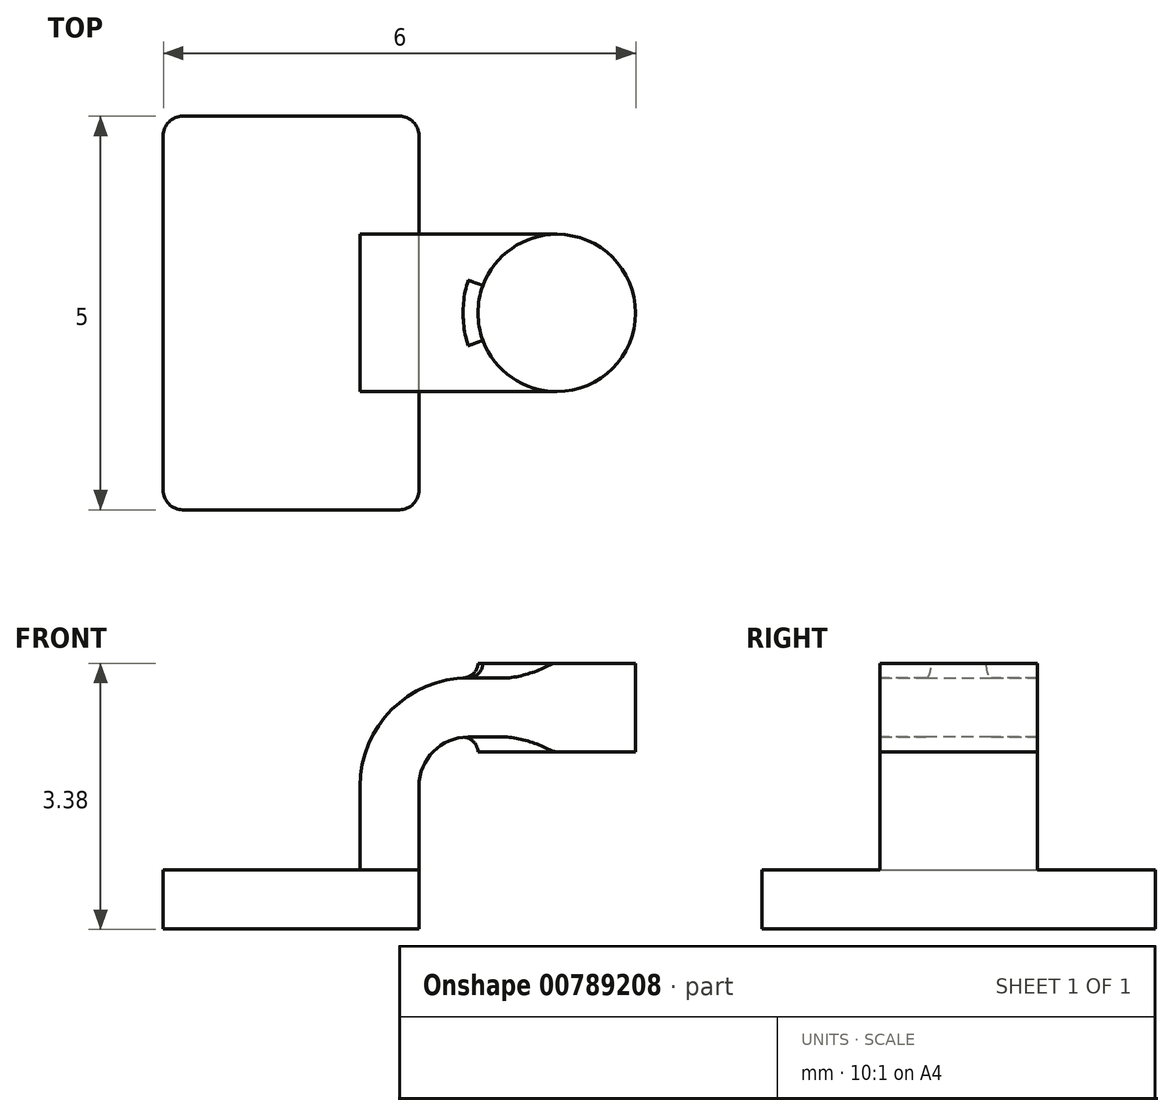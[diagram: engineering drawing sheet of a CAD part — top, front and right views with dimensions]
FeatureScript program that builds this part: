
annotation { "Feature Type Name" : "Feature", "Feature Type Description" : "" }
export const myFeature = defineFeature(function(context is Context, id is Id, definition is map)
    precondition{}
    {
        {
            var Q0;
            Q0=qCreatedBy(makeId("Front.planeOp"),FACE);
            var sketch = newSketch(context, id + "F0", { "sketchPlane" : qUnion([Q0])});
            skLineSegment(sketch, "E0.bottom", {"start": v(-1.63, 0.38) * mm, "end": v(1.63, 0.38) * mm});
            skLineSegment(sketch, "E0.top", {"start": v(-1.63, -0.38) * mm, "end": v(1.63, -0.38) * mm});
            skLineSegment(sketch, "E0.left", {"start": v(-1.62, 0.38) * mm, "end": v(-1.62, -0.38) * mm});
            skLineSegment(sketch, "E0.right", {"start": v(1.63, 0.37) * mm, "end": v(1.63, -0.38) * mm});
            skPoint(sketch, "E0.middle", {"position": v(0, 0) * mm});
            skLineSegment(sketch, "E1.bottom", {"start": v(4.38, 1.87) * mm, "end": v(2.38, 1.87) * mm});
            skLineSegment(sketch, "E1.top", {"start": v(4.37, 3) * mm, "end": v(2.38, 3) * mm});
            skLineSegment(sketch, "E1.left", {"start": v(4.38, 1.87) * mm, "end": v(4.37, 3) * mm});
            skLineSegment(sketch, "E1.right", {"start": v(2.38, 1.88) * mm, "end": v(2.38, 3) * mm});
            skPoint(sketch, "E1.middle", {"position": v(3.38, 2.44) * mm});
            skLineSegment(sketch, "E2", {"start": v(1.62, 0.38) * mm, "end": v(1.62, 1.44) * mm});
            skArc(sketch, "E3", {"start": v(1.62, 1.44) * mm, "mid": v(1.8, 1.88) * mm, "end": v(2.25, 2.06) * mm});
            skLineSegment(sketch, "E4", {"start": v(2.25, 2.06) * mm, "end": v(3.38, 2.06) * mm});
            skLineSegment(sketch, "E5.0", {"start": v(2.25, 2.81) * mm, "end": v(3.38, 2.81) * mm});
            skArc(sketch, "E5.1", {"start": v(0.87, 1.44) * mm, "mid": v(1.28, 2.41) * mm, "end": v(2.25, 2.81) * mm});
            skLineSegment(sketch, "E5.2", {"start": v(0.87, 0.38) * mm, "end": v(0.87, 1.44) * mm});
            skLineSegment(sketch, "E6", {"start": v(3.38, 1.87) * mm, "end": v(3.38, 3) * mm});
            skFitSpline(sketch, "E7", {"points": [v(-1.62, 0.38) * mm, v(2.25, 2.81) * mm], "startDerivative": vector(0.08, 3.8) * mm, "endDerivative": vector(8.07, -0.01) * mm});
            skSolve(sketch);
        }
        {
            var Q0;
            Q0=makeQuery(id+"F0.imprint","IMPRINT",FACE,{"disambiguationData":[TD([[makeQuery(id+"F0.imprint","IMPRINT",EDGE,{"derivedFrom":sQuery(id+"F0.wireOp",EDGE,"E0.top")}),1.0]])]});
            extrude(context, id + "F1", {"entities" : qUnion([Q0]), "endBound" : BoundingType.SYMMETRIC, "depth" : 5 * mm, "offsetDistance" : 25 * mm});
        }
        {
            var Q0;
            {var subQ1=sQuery(id+"F0.wireOp",EDGE,"E2");Q0=makeQuery(id+"F0.imprint","IMPRINT",FACE,{"disambiguationData":[TD([[makeQuery(id+"F0.imprint","IMPRINT",EDGE,{"derivedFrom":subQ1}),1.0]])]});}
            var Q1;
            {var subQ0=sQuery(id+"F0.wireOp",EDGE,"E4");var subQ1=sQuery(id+"F0.wireOp",EDGE,"E1.right");var subQ2=makeQuery(id+"F0.imprint","INTERSECT",VERTEX,{"derivedFrom":[subQ1,subQ0]});Q1=makeQuery(id+"F0.imprint","IMPRINT",FACE,{"disambiguationData":[TD([[makeQuery(id+"F0.imprint","IMPRINT",EDGE,{"disambiguationData":[TD([[subQ2,-1.0]])],"derivedFrom":subQ1}),-1.0]])]});}
            extrude(context, id + "F2", {"entities" : qUnion([Q0, Q1]), "operationType" : NewBodyOperationType.ADD, "endBound" : BoundingType.SYMMETRIC, "depth" : 2 * mm, "offsetDistance" : 25 * mm});
        }
        {
            var Q0;
            Q0=makeQuery(id+"F0.imprint","IMPRINT",FACE,{"disambiguationData":[TD([[makeQuery(id+"F0.imprint","IMPRINT",EDGE,{"derivedFrom":sQuery(id+"F0.wireOp",EDGE,"E5.1")}),1.0]])]});
            extrude(context, id + "F3", {"entities" : qUnion([Q0]), "operationType" : NewBodyOperationType.ADD, "endBound" : BoundingType.SYMMETRIC, "depth" : 0.62 * mm, "offsetDistance" : 25 * mm});
        }
        {
            var Q0;
            {var subQ4=sQuery(id+"F0.wireOp",EDGE,"E1.left");Q0=makeQuery(id+"F0.imprint","IMPRINT",FACE,{"disambiguationData":[TD([[makeQuery(id+"F0.imprint","IMPRINT",EDGE,{"derivedFrom":subQ4}),1.0]])]});}
            var Q1;
            Q1=sQuery(id+"F0.wireOp",EDGE,"E6");
            revolve(context, id + "F4", {"operationType" : NewBodyOperationType.ADD, "surfaceOperationType" : NewSurfaceOperationType.NEW, "entities" : qUnion([Q0]), "axis" : qUnion([Q1]), "revolveType" : RevolveType.FULL});
        }
        {
            var Q0;
            Q0=makeQuery(id+"F1.opExtrude","CAP_EDGE",EDGE,{"disambiguationData":[OSD([sQuery(id+"F0.wireOp",EDGE,"E0.right")])],"isStart":false});
            var Q1;
            Q1=makeQuery(id+"F1.opExtrude","CAP_EDGE",EDGE,{"disambiguationData":[OSD([sQuery(id+"F0.wireOp",EDGE,"E0.left")])],"isStart":false});
            var Q2;
            Q2=makeQuery(id+"F1.opExtrude","CAP_EDGE",EDGE,{"disambiguationData":[OSD([sQuery(id+"F0.wireOp",EDGE,"E0.right")])],"isStart":true});
            var Q3;
            Q3=makeQuery(id+"F1.opExtrude","CAP_EDGE",EDGE,{"disambiguationData":[OSD([sQuery(id+"F0.wireOp",EDGE,"E0.left")])],"isStart":true});
            var Q4;
            Q4=makeQuery(id+"F3.opExtrude","CAP_EDGE",EDGE,{"disambiguationData":[OSD([sQuery(id+"F0.wireOp",EDGE,"E5.2")])],"isStart":false});
            var Q5;
            Q5=makeQuery(id+"F3.opExtrude","CAP_EDGE",EDGE,{"disambiguationData":[OSD([sQuery(id+"F0.wireOp",EDGE,"E0.bottom")])],"isStart":false});
            var Q6;
            {var subQ0=sQuery(id+"F0.wireOp",EDGE,"E0.bottom");var subQ1=sQuery(id+"F0.wireOp",EDGE,"E5.2");var subQ2=sQuery(id+"F0.wireOp",EDGE,"E5.1");Q6=makeQuery(id+"F3.boolean.opBoolean","SPLIT",EDGE,{"disambiguationData":[TD([makeQuery(id+"F3.opExtrude","CAP_FACE",FACE,{"disambiguationData":[OSD([subQ0,subQ2,subQ1,sQuery(id+"F0.wireOp",EDGE,"E7")])],"isStart":false})])],"derivedFrom":makeQuery(id+"F2.opExtrude","SWEPT_EDGE",EDGE,{"disambiguationData":[OSD([subQ0,subQ1])]})});}
            var Q7;
            Q7=makeQuery(id+"F2.opExtrude","CAP_EDGE",EDGE,{"disambiguationData":[OSD([sQuery(id+"F0.wireOp",EDGE,"E0.bottom")])],"isStart":false});
            var Q8;
            Q8=makeQuery(id+"F3.opExtrude","CAP_EDGE",EDGE,{"disambiguationData":[OSD([sQuery(id+"F0.wireOp",EDGE,"E5.2")])],"isStart":true});
            var Q9;
            Q9=makeQuery(id+"F3.opExtrude","CAP_EDGE",EDGE,{"disambiguationData":[OSD([sQuery(id+"F0.wireOp",EDGE,"E0.bottom")])],"isStart":true});
            var Q10;
            Q10=makeQuery(id+"F2.opExtrude","CAP_EDGE",EDGE,{"disambiguationData":[OSD([sQuery(id+"F0.wireOp",EDGE,"E0.bottom")])],"isStart":true});
            var Q11;
            {var subQ0=sQuery(id+"F0.wireOp",EDGE,"E0.bottom");var subQ1=sQuery(id+"F0.wireOp",EDGE,"E5.2");var subQ2=sQuery(id+"F0.wireOp",EDGE,"E5.1");Q11=makeQuery(id+"F3.boolean.opBoolean","SPLIT",EDGE,{"disambiguationData":[TD([makeQuery(id+"F3.opExtrude","CAP_FACE",FACE,{"disambiguationData":[OSD([subQ0,subQ2,subQ1,sQuery(id+"F0.wireOp",EDGE,"E7")])],"isStart":true})])],"derivedFrom":makeQuery(id+"F2.opExtrude","SWEPT_EDGE",EDGE,{"disambiguationData":[OSD([subQ0,subQ1])]})});}
            fillet(context, id + "F5", {"entities" : qUnion([Q0, Q1, Q2, Q3, Q4, Q5, Q6, Q7, Q8, Q9, Q10, Q11]), "radius" : 0.25 * mm, "tangentPropagation" : true, "allowEdgeOverflow" : false});
        }
        {
            var Q0;
            Q0=makeQuery(id+"F4.boolean.opBoolean","INTERSECT",EDGE,{"derivedFrom":[makeQuery(id+"F2.opExtrude","SWEPT_FACE",FACE,{"disambiguationData":[OSD([sQuery(id+"F0.wireOp",EDGE,"E5.0")])]}),makeQuery(id+"F4.opRevolve","SWEPT_FACE",FACE,{"disambiguationData":[OSD([sQuery(id+"F0.wireOp",EDGE,"E1.left")])]})]});
            var Q1;
            Q1=makeQuery(id+"F4.boolean.opBoolean","INTERSECT",EDGE,{"derivedFrom":[makeQuery(id+"F2.opExtrude","SWEPT_FACE",FACE,{"disambiguationData":[OSD([sQuery(id+"F0.wireOp",EDGE,"E4")])]}),makeQuery(id+"F4.opRevolve","SWEPT_FACE",FACE,{"disambiguationData":[OSD([sQuery(id+"F0.wireOp",EDGE,"E1.left")])]})]});
            fillet(context, id + "F6", {"entities" : qUnion([Q0, Q1]), "radius" : 0.2 * mm, "tangentPropagation" : true, "allowEdgeOverflow" : false});
        }
    });
